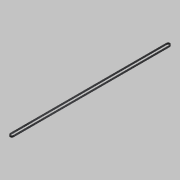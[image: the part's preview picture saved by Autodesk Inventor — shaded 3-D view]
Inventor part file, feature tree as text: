
AUTODESK INVENTOR PART (.ipt)
format: ipt  version: 2014 (Build 180170000, 170)  size: 78,848 bytes
history: native  units: mm
features: extrude x1, sketch x1, reference x1
ambient origin geometry x8: Origin, YZ Plane, XZ Plane, XY Plane, X Axis, Y Axis, Z Axis, Center Point
bodies: Solid1 (feature_tree)
feature tree (3):
  extrude  "Extrusion1"  Depth=6.0mm TaperAngle=0.0deg
  sketch  "Sketch1"  dims[d0=1.5mm d1=6.0mm d2=0.0mm d3=573.0mm d4=0.0mm]
  reference  "Reference3"
